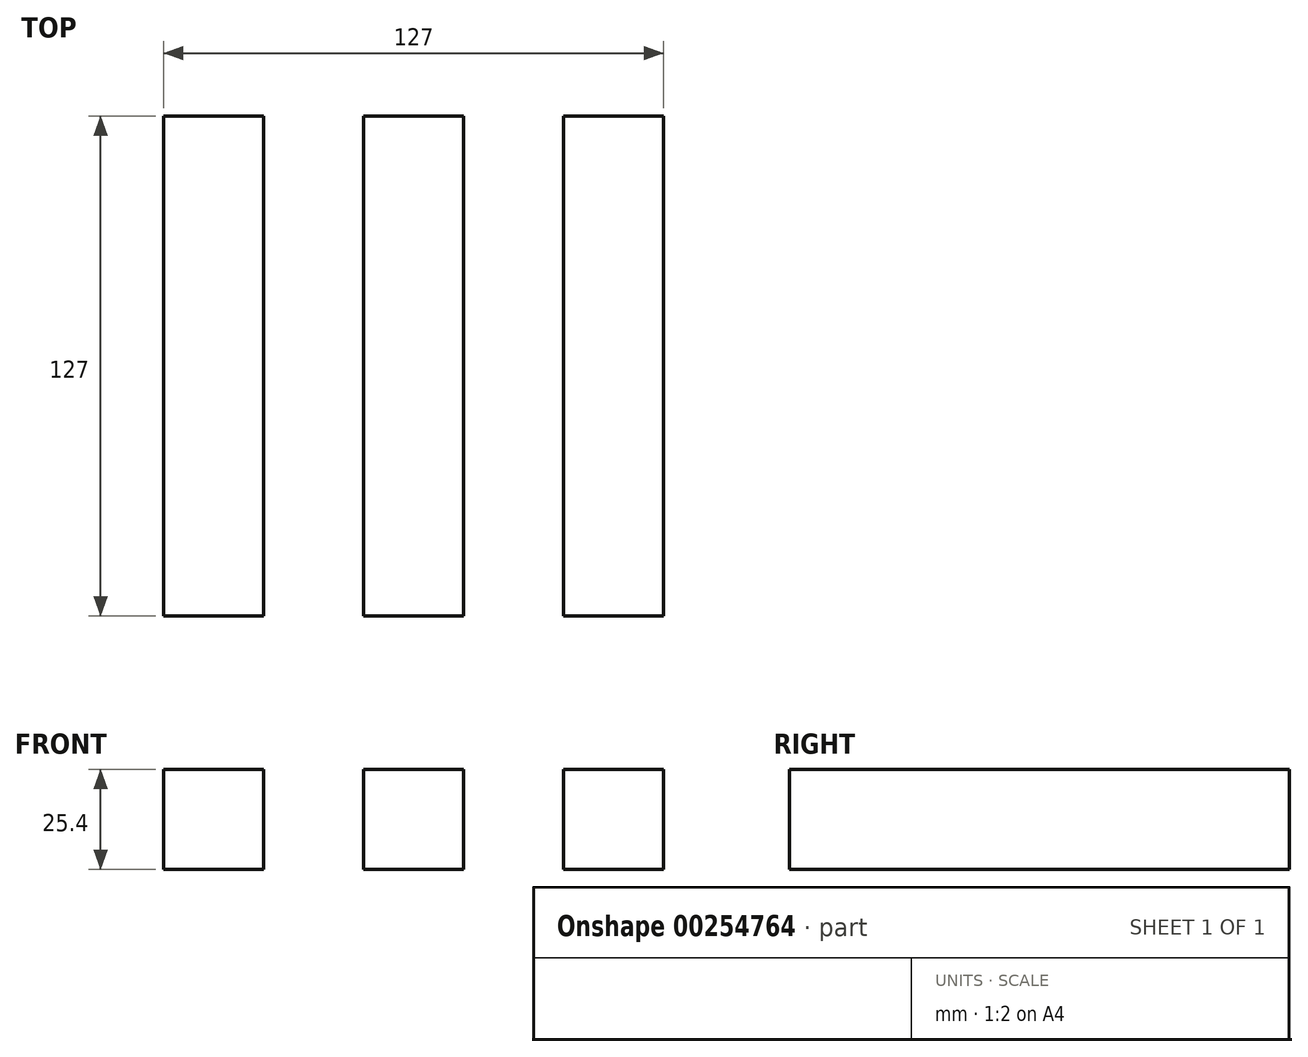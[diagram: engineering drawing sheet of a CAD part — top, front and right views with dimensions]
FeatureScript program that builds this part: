
annotation { "Feature Type Name" : "Feature", "Feature Type Description" : "" }
export const myFeature = defineFeature(function(context is Context, id is Id, definition is map)
    precondition{}
    {
        {
            var Q0;
            Q0=qCreatedBy(makeId("Front.planeOp"),FACE);
            var sketch = newSketch(context, id + "F0", { "sketchPlane" : qUnion([Q0])});
            skLineSegment(sketch, "E0.bottom", {"start": v(12.7, -12.7) * mm, "end": v(-12.7, -12.7) * mm});
            skLineSegment(sketch, "E0.top", {"start": v(12.7, 12.7) * mm, "end": v(-12.7, 12.7) * mm});
            skLineSegment(sketch, "E0.left", {"start": v(12.7, -12.7) * mm, "end": v(12.7, 12.7) * mm});
            skLineSegment(sketch, "E0.right", {"start": v(-12.7, -12.7) * mm, "end": v(-12.7, 12.7) * mm});
            skPoint(sketch, "E0.middle", {"position": v(0, 0) * mm});
            skPoint(sketch, "E1.endSnap0", {"position": v(12.7, 0) * mm});
            skPoint(sketch, "E2.endSnap0", {"position": v(-12.7, 0) * mm});
            skLineSegment(sketch, "E3.bottom", {"start": v(63.5, -12.7) * mm, "end": v(38.1, -12.7) * mm});
            skLineSegment(sketch, "E3.top", {"start": v(63.5, 12.7) * mm, "end": v(38.1, 12.7) * mm});
            skLineSegment(sketch, "E3.left", {"start": v(63.5, -12.7) * mm, "end": v(63.5, 12.7) * mm});
            skLineSegment(sketch, "E3.right", {"start": v(38.1, -12.7) * mm, "end": v(38.1, 12.7) * mm});
            skPoint(sketch, "E3.middle", {"position": v(50.8, 0) * mm});
            skLineSegment(sketch, "E4.bottom", {"start": v(-63.5, -12.7) * mm, "end": v(-38.1, -12.7) * mm});
            skLineSegment(sketch, "E4.top", {"start": v(-63.5, 12.7) * mm, "end": v(-38.1, 12.7) * mm});
            skLineSegment(sketch, "E4.left", {"start": v(-63.5, -12.7) * mm, "end": v(-63.5, 12.7) * mm});
            skLineSegment(sketch, "E4.right", {"start": v(-38.1, -12.7) * mm, "end": v(-38.1, 12.7) * mm});
            skPoint(sketch, "E4.middle", {"position": v(-50.8, 0) * mm});
            skLineSegment(sketch, "E5", {"start": v(-50.8, 0) * mm, "end": v(0, 0) * mm});
            skLineSegment(sketch, "E6", {"start": v(50.8, 0) * mm, "end": v(0, 0) * mm});
            skSolve(sketch);
        }
        {
            var Q0;
            {var subQ1=sQuery(id+"F0.wireOp",EDGE,"E3.bottom");Q0=makeQuery(id+"F0.imprint","IMPRINT",FACE,{"disambiguationData":[TD([[makeQuery(id+"F0.imprint","IMPRINT",EDGE,{"derivedFrom":subQ1}),-1.0]])]});}
            var Q1;
            {var subQ1=sQuery(id+"F0.wireOp",EDGE,"E0.top");Q1=makeQuery(id+"F0.imprint","IMPRINT",FACE,{"disambiguationData":[TD([[makeQuery(id+"F0.imprint","IMPRINT",EDGE,{"derivedFrom":subQ1}),1.0]])]});}
            var Q2;
            {var subQ1=sQuery(id+"F0.wireOp",EDGE,"E0.bottom");Q2=makeQuery(id+"F0.imprint","IMPRINT",FACE,{"disambiguationData":[TD([[makeQuery(id+"F0.imprint","IMPRINT",EDGE,{"derivedFrom":subQ1}),-1.0]])]});}
            var Q3;
            {var subQ1=sQuery(id+"F0.wireOp",EDGE,"E4.bottom");Q3=makeQuery(id+"F0.imprint","IMPRINT",FACE,{"disambiguationData":[TD([[makeQuery(id+"F0.imprint","IMPRINT",EDGE,{"derivedFrom":subQ1}),1.0]])]});}
            extrude(context, id + "F1", {"entities" : qUnion([Q0, Q1, Q2, Q3]), "endBound" : BoundingType.SYMMETRIC, "depth" : 127 * mm});
        }
    });
